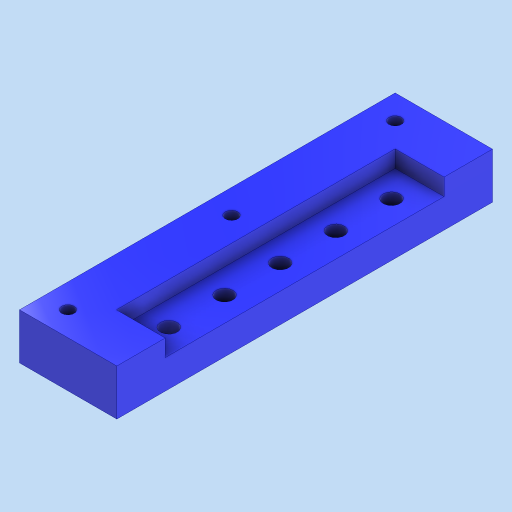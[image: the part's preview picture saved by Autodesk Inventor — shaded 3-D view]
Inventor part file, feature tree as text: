
AUTODESK INVENTOR PART (.ipt)
format: ipt  version: 2023 (Build 270158000, 158)  size: 168,448 bytes
history: native  units: in
note: dims shown in document units (in); Inventor stores cm internally (conversion verified against a paired STEP export)
features: extrude x3, other x1, sketch x1
ambient origin geometry x8: Origin, YZ Plane, XZ Plane, XY Plane, X Axis, Y Axis, Z Axis, Center Point
bodies: Solid1 (feature_tree)
feature tree (5):
  parser-record x1  (decoder bookkeeping rows leaked as tree rows — omitted from the tree; the rows remain in map.json)
  sketch  "Sketch1"  dims[d0=4.5354in d1=0.7953in d2=0.2756in d3=0.9055in d4=0.9055in d5=0.4724in d6=0.0in d7=0.0787in d8=0.0in d9=0.748in d10=0.0in d11=0.7874in d12=0.7874in d13=0.7874in d14=0.2047in]
  extrude  "Extrusion1"  Depth=0.7953in
  extrude  "Extrusion2"  Depth=0.2756in
  extrude  "Extrusion3"  Depth=0.7874in
note: 1 file-system path scrubbed to <path> (originals preserved in map.json)
